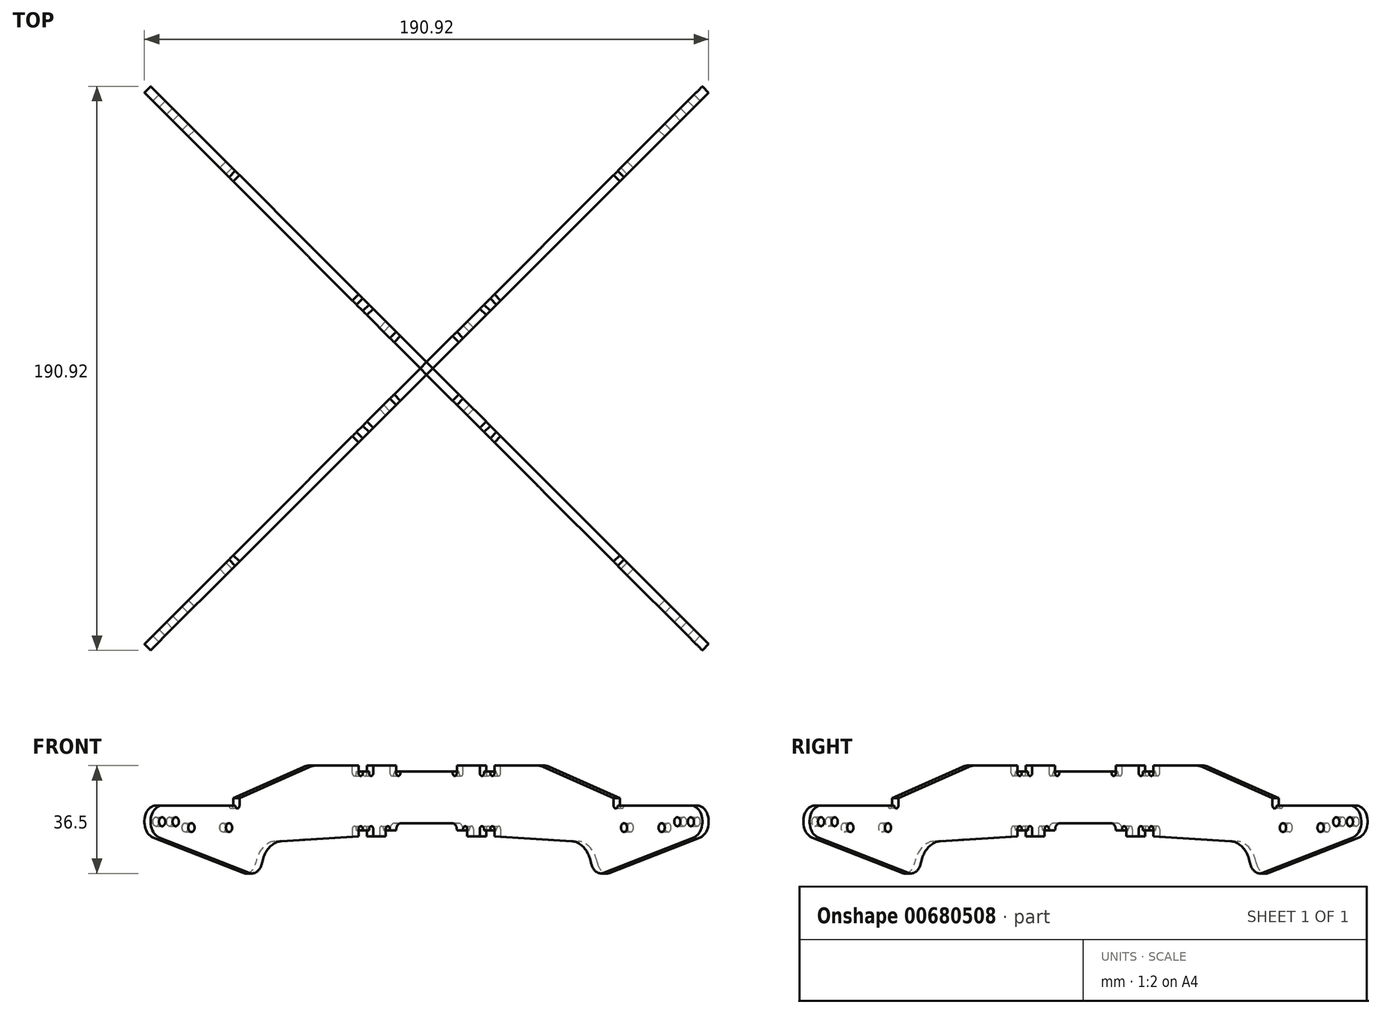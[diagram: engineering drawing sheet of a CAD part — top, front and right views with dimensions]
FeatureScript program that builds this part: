
annotation { "Feature Type Name" : "Feature", "Feature Type Description" : "" }
export const myFeature = defineFeature(function(context is Context, id is Id, definition is map)
    precondition{}
    {
        {
            var Q0;
            Q0=qCreatedBy(makeId("Front.planeOp"),FACE);
            var sketch = newSketch(context, id + "F0", { "sketchPlane" : qUnion([Q0])});
            skLineSegment(sketch, "E0", {"start": v(0, 0) * mm, "end": v(0, 165.72) * mm, "construction": true});
            skSolve(sketch);
        }
        {
            var Q0;
            Q0=qCreatedBy(makeId("Front.planeOp"),FACE);
            var Q1;
            Q1=sQuery(id+"F0.wireOp",EDGE,"E0");
            cPlane(context, id + "F1", {"entities" : qUnion([Q0, Q1]), "cplaneType" : CPlaneType.LINE_ANGLE, "offset" : 25 * mm, "angle" : 45 * degree, "oppositeDirection" : true, "width" : 150 * mm, "height" : 150 * mm});
        }
        {
            var Q0;
            Q0=qCreatedBy(id+"F1.planeOp",FACE);
            var sketch = newSketch(context, id + "F2", { "sketchPlane" : qUnion([Q0])});
            skLineSegment(sketch, "E1", {"start": v(16, 0) * mm, "end": v(19, 0) * mm});
            skLineSegment(sketch, "E2", {"start": v(19, 0) * mm, "end": v(19, 0.5) * mm});
            skLineSegment(sketch, "E3", {"start": v(21, 0.5) * mm, "end": v(21, -2) * mm});
            skLineSegment(sketch, "E4", {"start": v(21, -2) * mm, "end": v(27, -2) * mm});
            skLineSegment(sketch, "E5", {"start": v(27, -2) * mm, "end": v(27, 0.5) * mm});
            skLineSegment(sketch, "E6", {"start": v(29, 0.5) * mm, "end": v(29, 0) * mm});
            skLineSegment(sketch, "E7", {"start": v(29, 0) * mm, "end": v(32, 0) * mm});
            skLineSegment(sketch, "E8", {"start": v(32, 0) * mm, "end": v(32, 0.5) * mm});
            skLineSegment(sketch, "E9", {"start": v(34, 0.5) * mm, "end": v(34, -2) * mm});
            skLineSegment(sketch, "E10", {"start": v(34, -2) * mm, "end": v(71, -3.6) * mm});
            skLineSegment(sketch, "E11", {"start": v(-16, 0) * mm, "end": v(-19, 0) * mm});
            skLineSegment(sketch, "E12", {"start": v(-19, 0) * mm, "end": v(-19, 0.5) * mm});
            skLineSegment(sketch, "E13", {"start": v(-21, 0.5) * mm, "end": v(-21, -2) * mm});
            skLineSegment(sketch, "E14", {"start": v(-21, -2) * mm, "end": v(-27, -2) * mm});
            skLineSegment(sketch, "E15", {"start": v(-27, -2) * mm, "end": v(-27, 0.5) * mm});
            skLineSegment(sketch, "E16", {"start": v(-29, 0.5) * mm, "end": v(-29, 0) * mm});
            skLineSegment(sketch, "E17", {"start": v(-29, 0) * mm, "end": v(-32, 0) * mm});
            skLineSegment(sketch, "E18", {"start": v(-32, 0) * mm, "end": v(-32, 0.5) * mm});
            skLineSegment(sketch, "E19", {"start": v(-34, 0.5) * mm, "end": v(-34, -2) * mm});
            skLineSegment(sketch, "E20", {"start": v(16, 0) * mm, "end": v(16, 0.25) * mm});
            skPoint(sketch, "E21.end.orphan", {"position": v(-16, 2.5) * mm});
            skLineSegment(sketch, "E22", {"start": v(13.75, 2.5) * mm, "end": v(-13.75, 2.5) * mm});
            skLineSegment(sketch, "E23", {"start": v(-16, 0) * mm, "end": v(-16, 0.25) * mm});
            skArc(sketch, "E24", {"start": v(29, 0.5) * mm, "mid": v(28, 1.5) * mm, "end": v(27, 0.5) * mm});
            skArc(sketch, "E25", {"start": v(34, 0.5) * mm, "mid": v(33, 1.5) * mm, "end": v(32, 0.5) * mm});
            skLineSegment(sketch, "E26", {"start": v(18.64, 0.5) * mm, "end": v(35.36, 0.5) * mm, "construction": true});
            skArc(sketch, "E27", {"start": v(21, 0.5) * mm, "mid": v(20, 1.5) * mm, "end": v(19, 0.5) * mm});
            skLineSegment(sketch, "E28", {"start": v(-35.97, 0.5) * mm, "end": v(-19, 0.5) * mm, "construction": true});
            skArc(sketch, "E29", {"start": v(-19, 0.5) * mm, "mid": v(-20, 1.5) * mm, "end": v(-21, 0.5) * mm});
            skArc(sketch, "E30", {"start": v(-27, 0.5) * mm, "mid": v(-28, 1.5) * mm, "end": v(-29, 0.5) * mm});
            skArc(sketch, "E31", {"start": v(-32, 0.5) * mm, "mid": v(-33, 1.5) * mm, "end": v(-34, 0.5) * mm});
            skPoint(sketch, "E32.visualSharp", {"position": v(16, 2.5) * mm});
            skArc(sketch, "E32.filletArc", {"start": v(16, 0.25) * mm, "mid": v(15.34, 1.84) * mm, "end": v(13.75, 2.5) * mm});
            skArc(sketch, "E33.filletArc", {"start": v(-13.75, 2.5) * mm, "mid": v(-15.34, 1.84) * mm, "end": v(-16, 0.25) * mm});
            skLineSegment(sketch, "E34", {"start": v(14, 20) * mm, "end": v(-14, 20) * mm});
            skLineSegment(sketch, "E35", {"start": v(8.96, 19.5) * mm, "end": v(35.36, 19.5) * mm, "construction": true});
            skLineSegment(sketch, "E36", {"start": v(29, 19.5) * mm, "end": v(29, 20) * mm});
            skLineSegment(sketch, "E37", {"start": v(32, 19.5) * mm, "end": v(32, 20) * mm});
            skLineSegment(sketch, "E38", {"start": v(34, 19.5) * mm, "end": v(34, 22) * mm});
            skLineSegment(sketch, "E39", {"start": v(27, 19.5) * mm, "end": v(27, 22) * mm});
            skLineSegment(sketch, "E40", {"start": v(-10.2, 19.5) * mm, "end": v(-35.97, 19.5) * mm, "construction": true});
            skLineSegment(sketch, "E41", {"start": v(-34, 19.5) * mm, "end": v(-34, 22) * mm});
            skLineSegment(sketch, "E42", {"start": v(-32, 19.5) * mm, "end": v(-32, 20) * mm});
            skLineSegment(sketch, "E43", {"start": v(-29, 19.5) * mm, "end": v(-29, 20) * mm});
            skLineSegment(sketch, "E44", {"start": v(-27, 19.5) * mm, "end": v(-27, 22) * mm});
            skArc(sketch, "E45", {"start": v(32, 19.5) * mm, "mid": v(33, 18.5) * mm, "end": v(34, 19.5) * mm});
            skArc(sketch, "E46", {"start": v(29, 19.5) * mm, "mid": v(28, 18.5) * mm, "end": v(27, 19.5) * mm});
            skArc(sketch, "E47", {"start": v(-27, 19.5) * mm, "mid": v(-28, 18.5) * mm, "end": v(-29, 19.5) * mm});
            skArc(sketch, "E48", {"start": v(-32, 19.5) * mm, "mid": v(-33, 18.5) * mm, "end": v(-34, 19.5) * mm});
            skLineSegment(sketch, "E49", {"start": v(-32, 20) * mm, "end": v(-29, 20) * mm});
            skLineSegment(sketch, "E50", {"start": v(29, 20) * mm, "end": v(32, 20) * mm});
            skLineSegment(sketch, "E51", {"start": v(-14, 20) * mm, "end": v(-14, 19.5) * mm});
            skLineSegment(sketch, "E52", {"start": v(14, 20) * mm, "end": v(14, 19.5) * mm});
            skArc(sketch, "E53", {"start": v(14, 19.5) * mm, "mid": v(15, 18.5) * mm, "end": v(16, 19.5) * mm});
            skLineSegment(sketch, "E54", {"start": v(16, 19.5) * mm, "end": v(16, 22) * mm});
            skLineSegment(sketch, "E55", {"start": v(16, 22) * mm, "end": v(27, 22) * mm});
            skLineSegment(sketch, "E56", {"start": v(-16, 22) * mm, "end": v(-16, 19.5) * mm});
            skArc(sketch, "E57", {"start": v(-14, 19.5) * mm, "mid": v(-15, 18.5) * mm, "end": v(-16, 19.5) * mm});
            skLineSegment(sketch, "E58", {"start": v(-27, 22) * mm, "end": v(-16, 22) * mm});
            skLineSegment(sketch, "E59", {"start": v(34, 22) * mm, "end": v(54.47, 22) * mm});
            skLineSegment(sketch, "E60", {"start": v(-34, 22) * mm, "end": v(-54.47, 22) * mm});
            skLineSegment(sketch, "E61", {"start": v(93, 8.5) * mm, "end": v(128, 8.5) * mm});
            skLineSegment(sketch, "E62", {"start": v(-93, 8.5) * mm, "end": v(-128, 8.5) * mm});
            skLineSegment(sketch, "E63", {"start": v(57.46, 21.54) * mm, "end": v(91, 11) * mm});
            skArc(sketch, "E64", {"start": v(93, 8.5) * mm, "mid": v(92, 7.5) * mm, "end": v(91, 8.5) * mm});
            skLineSegment(sketch, "E65", {"start": v(91, 8.5) * mm, "end": v(91, 11) * mm});
            skLineSegment(sketch, "E66", {"start": v(129.48, -2.3) * mm, "end": v(86.34, -14.32) * mm});
            skArc(sketch, "E67", {"start": v(129.48, -2.3) * mm, "mid": v(133.45, 3.74) * mm, "end": v(128, 8.5) * mm});
            skPoint(sketch, "E68.orphan", {"position": v(137.72, 0) * mm});
            skLineSegment(sketch, "E69", {"start": v(105, 28.31) * mm, "end": v(105, -17.87) * mm, "construction": true});
            skPoint(sketch, "E70.visualSharp", {"position": v(56, 22) * mm});
            skArc(sketch, "E70.filletArc", {"start": v(57.46, 21.54) * mm, "mid": v(55.98, 21.88) * mm, "end": v(54.47, 22) * mm});
            skArc(sketch, "E71", {"start": v(80.2, -10.87) * mm, "mid": v(82.55, -13.86) * mm, "end": v(86.34, -14.32) * mm});
            skLineSegment(sketch, "E72", {"start": v(-105, 28.31) * mm, "end": v(-105, -17.87) * mm, "construction": true});
            skArc(sketch, "E73", {"start": v(-54.47, 22) * mm, "mid": v(-55.98, 21.88) * mm, "end": v(-57.46, 21.54) * mm});
            skArc(sketch, "E74", {"start": v(-91, 8.5) * mm, "mid": v(-92, 7.5) * mm, "end": v(-93, 8.5) * mm});
            skArc(sketch, "E75", {"start": v(-128, 8.5) * mm, "mid": v(-133.45, 3.74) * mm, "end": v(-129.48, -2.3) * mm});
            skLineSegment(sketch, "E76", {"start": v(-129.48, -2.3) * mm, "end": v(-86.34, -14.32) * mm});
            skArc(sketch, "E77", {"start": v(-86.34, -14.32) * mm, "mid": v(-82.55, -13.86) * mm, "end": v(-80.2, -10.87) * mm});
            skCircle(sketch, "E78", {"center": v(128, 3) * mm, "radius": 1.5 * mm});
            skCircle(sketch, "E79", {"center": v(-128, 3) * mm, "radius": 1.5 * mm});
            skCircle(sketch, "E80", {"center": v(121.5, 3) * mm, "radius": 1.5 * mm});
            skCircle(sketch, "E81", {"center": v(-121.5, 3) * mm, "radius": 1.5 * mm});
            skCircle(sketch, "E82", {"center": v(114, 1) * mm, "radius": 1.5 * mm});
            skCircle(sketch, "E83", {"center": v(96, 1) * mm, "radius": 1.5 * mm});
            skCircle(sketch, "E84", {"center": v(-96, 1) * mm, "radius": 1.5 * mm});
            skCircle(sketch, "E85", {"center": v(-114, 1) * mm, "radius": 1.5 * mm});
            skLineSegment(sketch, "E86", {"start": v(114, 1) * mm, "end": v(96, 1) * mm, "construction": true});
            skLineSegment(sketch, "E87", {"start": v(-96, 1) * mm, "end": v(-114, 1) * mm, "construction": true});
            skArc(sketch, "E88", {"start": v(-71, -3.6) * mm, "mid": v(-76.77, -5.75) * mm, "end": v(-80.2, -10.87) * mm});
            skArc(sketch, "E89", {"start": v(80.2, -10.87) * mm, "mid": v(76.77, -5.75) * mm, "end": v(71, -3.6) * mm});
            skLineSegment(sketch, "E90", {"start": v(-34, -2) * mm, "end": v(-71, -3.6) * mm});
            skLineSegment(sketch, "E91", {"start": v(-57.46, 21.54) * mm, "end": v(-91, 11) * mm});
            skLineSegment(sketch, "E92", {"start": v(-91, 8.5) * mm, "end": v(-91, 11) * mm});
            skPoint(sketch, "E93.firstSnap0", {"position": v(27, 0.5) * mm});
            skSolve(sketch);
        }
        {
            var Q0;
            Q0=makeQuery(id+"F2.imprint","IMPRINT",FACE,{"disambiguationData":[TD([[makeQuery(id+"F2.imprint","IMPRINT",EDGE,{"derivedFrom":sQuery(id+"F2.wireOp",EDGE,"E1")}),1.0]])]});
            extrude(context, id + "F3", {"entities" : qUnion([Q0]), "endBound" : BoundingType.SYMMETRIC, "depth" : 3 * mm, "offsetDistance" : 25 * mm});
        }
        {
            var Q0;
            Q0=makeQuery(id+"F3.opExtrude","SWEPT_BODY",BODY,{"disambiguationData":[OSD([sQuery(id+"F2.wireOp",EDGE,"E1"),sQuery(id+"F2.wireOp",EDGE,"E2"),sQuery(id+"F2.wireOp",EDGE,"E3"),sQuery(id+"F2.wireOp",EDGE,"E4"),sQuery(id+"F2.wireOp",EDGE,"E5"),sQuery(id+"F2.wireOp",EDGE,"E6"),sQuery(id+"F2.wireOp",EDGE,"E7"),sQuery(id+"F2.wireOp",EDGE,"E8"),sQuery(id+"F2.wireOp",EDGE,"E9"),sQuery(id+"F2.wireOp",EDGE,"E10"),sQuery(id+"F2.wireOp",EDGE,"E11"),sQuery(id+"F2.wireOp",EDGE,"E12"),sQuery(id+"F2.wireOp",EDGE,"E13"),sQuery(id+"F2.wireOp",EDGE,"E14"),sQuery(id+"F2.wireOp",EDGE,"E15"),sQuery(id+"F2.wireOp",EDGE,"E16"),sQuery(id+"F2.wireOp",EDGE,"E17"),sQuery(id+"F2.wireOp",EDGE,"E18"),sQuery(id+"F2.wireOp",EDGE,"E19"),sQuery(id+"F2.wireOp",EDGE,"4rOWkPbb-RmEL-z8Lk-gB0e-ePXBMJ1WBncx"),sQuery(id+"F2.wireOp",EDGE,"E20"),sQuery(id+"F2.wireOp",EDGE,"E22"),sQuery(id+"F2.wireOp",EDGE,"E23"),sQuery(id+"F2.wireOp",EDGE,"E24"),sQuery(id+"F2.wireOp",EDGE,"E25"),sQuery(id+"F2.wireOp",EDGE,"E27"),sQuery(id+"F2.wireOp",EDGE,"E29"),sQuery(id+"F2.wireOp",EDGE,"E30"),sQuery(id+"F2.wireOp",EDGE,"E31"),sQuery(id+"F2.wireOp",EDGE,"E32.filletArc"),sQuery(id+"F2.wireOp",EDGE,"E33.filletArc"),sQuery(id+"F2.wireOp",EDGE,"E34"),sQuery(id+"F2.wireOp",EDGE,"E36"),sQuery(id+"F2.wireOp",EDGE,"E37"),sQuery(id+"F2.wireOp",EDGE,"E38"),sQuery(id+"F2.wireOp",EDGE,"E39"),sQuery(id+"F2.wireOp",EDGE,"E41"),sQuery(id+"F2.wireOp",EDGE,"E42"),sQuery(id+"F2.wireOp",EDGE,"E43"),sQuery(id+"F2.wireOp",EDGE,"E44"),sQuery(id+"F2.wireOp",EDGE,"E45"),sQuery(id+"F2.wireOp",EDGE,"E46"),sQuery(id+"F2.wireOp",EDGE,"E47"),sQuery(id+"F2.wireOp",EDGE,"E48"),sQuery(id+"F2.wireOp",EDGE,"E49"),sQuery(id+"F2.wireOp",EDGE,"E50"),sQuery(id+"F2.wireOp",EDGE,"E51"),sQuery(id+"F2.wireOp",EDGE,"E52"),sQuery(id+"F2.wireOp",EDGE,"E53"),sQuery(id+"F2.wireOp",EDGE,"E54"),sQuery(id+"F2.wireOp",EDGE,"E55"),sQuery(id+"F2.wireOp",EDGE,"E56"),sQuery(id+"F2.wireOp",EDGE,"E57"),sQuery(id+"F2.wireOp",EDGE,"E58"),sQuery(id+"F2.wireOp",EDGE,"E59"),sQuery(id+"F2.wireOp",EDGE,"E60"),sQuery(id+"F2.wireOp",EDGE,"E61"),sQuery(id+"F2.wireOp",EDGE,"E62"),sQuery(id+"F2.wireOp",EDGE,"E63"),sQuery(id+"F2.wireOp",EDGE,"E64"),sQuery(id+"F2.wireOp",EDGE,"E65"),sQuery(id+"F2.wireOp",EDGE,"cf4ffc77-f907-45a9-80f5-f742178e28b2"),sQuery(id+"F2.wireOp",EDGE,"E66"),sQuery(id+"F2.wireOp",EDGE,"E67"),sQuery(id+"F2.wireOp",EDGE,"E70.filletArc"),sQuery(id+"F2.wireOp",EDGE,"EQCc0N98-a6pS-hrii-lUOX-8gSsFHNqvyFs"),sQuery(id+"F2.wireOp",EDGE,"E71"),sQuery(id+"F2.wireOp",EDGE,"WmwSjkpW-vMyV-Cnct-yn3w-nC6IyCHbTIQY"),sQuery(id+"F2.wireOp",EDGE,"Mew3nuBt-TA8Q-e68U-HJVp-KEopOIUlYbYa"),sQuery(id+"F2.wireOp",EDGE,"E73"),sQuery(id+"F2.wireOp",EDGE,"E74"),sQuery(id+"F2.wireOp",EDGE,"E75"),sQuery(id+"F2.wireOp",EDGE,"f44ae8ca-bd31-4121-bce2-2ef92dd9c884"),sQuery(id+"F2.wireOp",EDGE,"E76"),sQuery(id+"F2.wireOp",EDGE,"E77"),sQuery(id+"F2.wireOp",EDGE,"cTXLr0oU-G9Rs-vPAw-ZPU8-Ut2Q6AE9oT31"),sQuery(id+"F2.wireOp",EDGE,"E78"),sQuery(id+"F2.wireOp",EDGE,"E79"),sQuery(id+"F2.wireOp",EDGE,"E80"),sQuery(id+"F2.wireOp",EDGE,"E81"),sQuery(id+"F2.wireOp",EDGE,"E82"),sQuery(id+"F2.wireOp",EDGE,"E83"),sQuery(id+"F2.wireOp",EDGE,"E84"),sQuery(id+"F2.wireOp",EDGE,"E85")])]});
            var Q1;
            Q1=qCreatedBy(makeId("Right.planeOp"),FACE);
            mirror(context, id + "F4", {"entities" : qUnion([Q0]), "mirrorPlane" : qUnion([Q1])});
        }
    });
